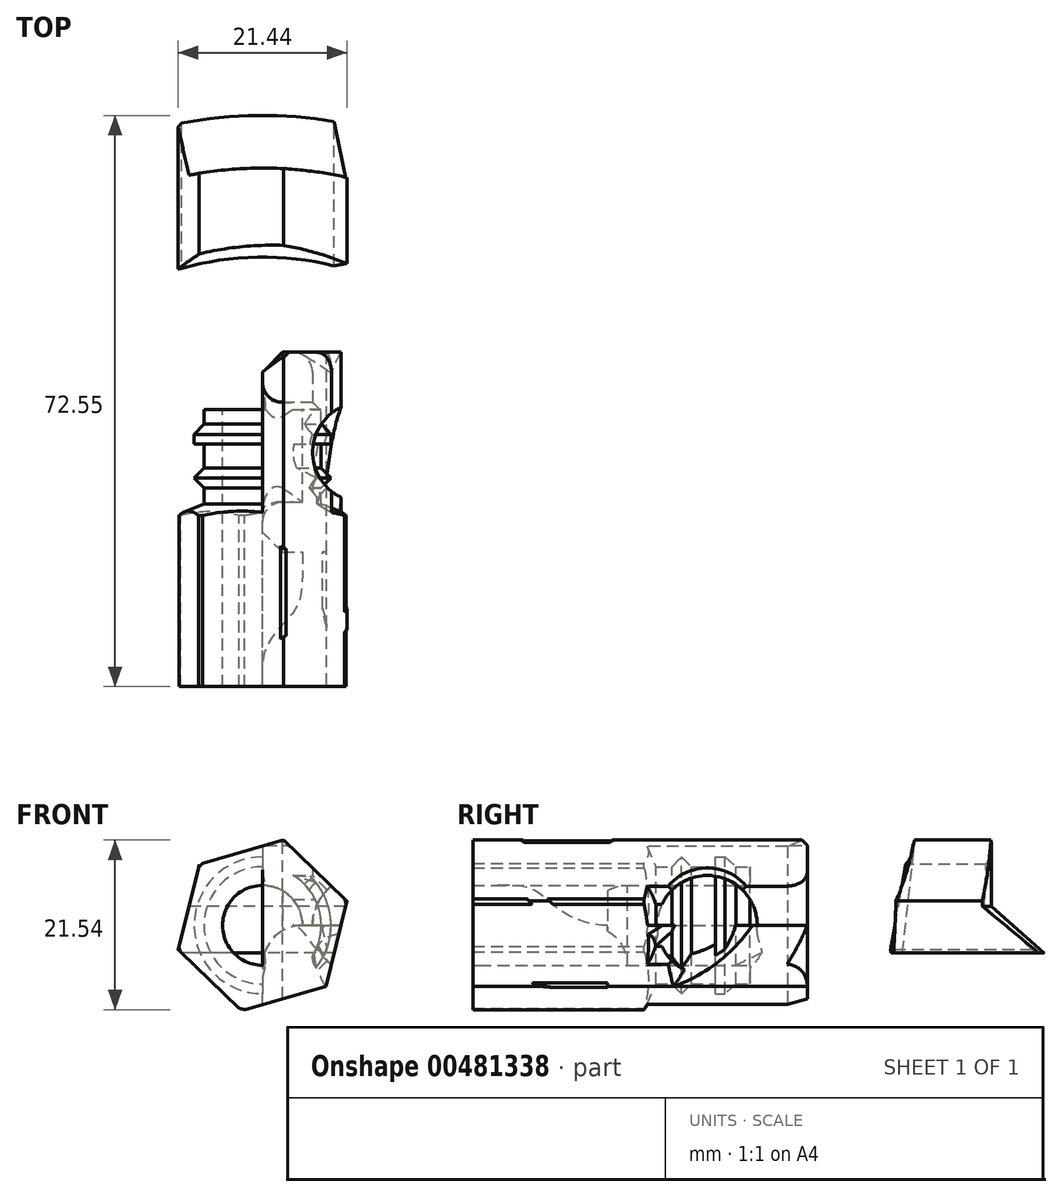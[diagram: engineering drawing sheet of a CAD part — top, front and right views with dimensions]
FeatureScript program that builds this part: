
annotation { "Feature Type Name" : "Feature", "Feature Type Description" : "" }
export const myFeature = defineFeature(function(context is Context, id is Id, definition is map)
    precondition{}
    {
        {
            var Q0;
            Q0=qCreatedBy(makeId("Top.planeOp"),FACE);
            var sketch = newSketch(context, id + "F0", { "sketchPlane" : qUnion([Q0])});
            skLineSegment(sketch, "E0.bottom", {"start": v(0, 0) * mm, "end": v(25.4, 0) * mm});
            skLineSegment(sketch, "E0.top", {"start": v(0, 25.4) * mm, "end": v(25.4, 25.4) * mm});
            skLineSegment(sketch, "E0.left", {"start": v(0, 0) * mm, "end": v(0, 25.4) * mm});
            skLineSegment(sketch, "E0.right", {"start": v(25.4, 0) * mm, "end": v(25.4, 25.4) * mm});
            skCircle(sketch, "E1", {"center": v(12.7, 12.7) * mm, "radius": 6.35 * mm});
            skPoint(sketch, "E1.centerSnap0", {"position": v(12.7, 0) * mm});
            skSolve(sketch);
        }
        {
            var Q0;
            Q0 = qSketchRegion(id + "F0", true);
            extrude(context, id + "F1", {"entities" : qUnion([Q0]), "endBound" : BoundingType.SYMMETRIC, "depth" : 25.4 * mm});
        }
        {
            var Q0;
            Q0=makeQuery(id+"F1.opExtrude","SWEPT_FACE",FACE,{"disambiguationData":[OSD([sQuery(id+"F0.wireOp",EDGE,"E0.right")])]});
            var sketch = newSketch(context, id + "F2", { "sketchPlane" : qUnion([Q0])});
            skCircle(sketch, "E2", {"center": v(12.7, 0) * mm, "radius": 6.35 * mm});
            skSolve(sketch);
        }
        {
            var Q0;
            Q0=makeQuery(id+"F2.imprint","IMPRINT",FACE,{"disambiguationData":[TD([[makeQuery(id+"F2.imprint","IMPRINT",EDGE,{"derivedFrom":sQuery(id+"F2.wireOp",EDGE,"E2")}),1.0]])]});
            extrude(context, id + "F3", {"entities" : qUnion([Q0]), "operationType" : NewBodyOperationType.REMOVE, "endBound" : BoundingType.THROUGH_ALL, "oppositeDirection" : true, "depth" : 25.4 * mm});
        }
        {
            var Q0;
            Q0=makeQuery(id+"F1.opExtrude","SWEPT_FACE",FACE,{"disambiguationData":[OSD([sQuery(id+"F0.wireOp",EDGE,"E0.bottom")])]});
            var sketch = newSketch(context, id + "F4", { "sketchPlane" : qUnion([Q0])});
            skCircle(sketch, "E3", {"center": v(12.7, 0) * mm, "radius": 6.35 * mm});
            skSolve(sketch);
        }
        {
            var Q0;
            Q0=makeQuery(id+"F4.imprint","IMPRINT",FACE,{"disambiguationData":[TD([[makeQuery(id+"F4.imprint","IMPRINT",EDGE,{"derivedFrom":sQuery(id+"F4.wireOp",EDGE,"E3")}),1.0]])]});
            extrude(context, id + "F5", {"entities" : qUnion([Q0]), "operationType" : NewBodyOperationType.REMOVE, "endBound" : BoundingType.THROUGH_ALL, "oppositeDirection" : true, "depth" : 25.4 * mm});
        }
        {
            var Q0;
            Q0=makeQuery(id+"F1.opExtrude","CAP_EDGE",EDGE,{"disambiguationData":[OSD([sQuery(id+"F0.wireOp",EDGE,"E0.bottom")])],"isStart":false});
            var Q1;
            Q1=makeQuery(id+"F1.opExtrude","CAP_EDGE",EDGE,{"disambiguationData":[OSD([sQuery(id+"F0.wireOp",EDGE,"E0.right")])],"isStart":false});
            var Q2;
            Q2=makeQuery(id+"F1.opExtrude","SWEPT_EDGE",EDGE,{"disambiguationData":[OSD([sQuery(id+"F0.wireOp",EDGE,"E0.bottom"),sQuery(id+"F0.wireOp",EDGE,"E0.right")])]});
            var Q3;
            Q3=makeQuery(id+"F1.opExtrude","CAP_EDGE",EDGE,{"disambiguationData":[OSD([sQuery(id+"F0.wireOp",EDGE,"E0.bottom")])],"isStart":true});
            var Q4;
            Q4=makeQuery(id+"F1.opExtrude","CAP_EDGE",EDGE,{"disambiguationData":[OSD([sQuery(id+"F0.wireOp",EDGE,"E0.right")])],"isStart":true});
            var Q5;
            Q5=makeQuery(id+"F1.opExtrude","SWEPT_EDGE",EDGE,{"disambiguationData":[OSD([sQuery(id+"F0.wireOp",EDGE,"E0.top"),sQuery(id+"F0.wireOp",EDGE,"E0.right")])]});
            var Q6;
            Q6=makeQuery(id+"F1.opExtrude","CAP_EDGE",EDGE,{"disambiguationData":[OSD([sQuery(id+"F0.wireOp",EDGE,"E0.top")])],"isStart":false});
            var Q7;
            Q7=makeQuery(id+"F1.opExtrude","SWEPT_EDGE",EDGE,{"disambiguationData":[OSD([sQuery(id+"F0.wireOp",EDGE,"E0.top"),sQuery(id+"F0.wireOp",EDGE,"E0.left")])]});
            var Q8;
            Q8=makeQuery(id+"F1.opExtrude","CAP_EDGE",EDGE,{"disambiguationData":[OSD([sQuery(id+"F0.wireOp",EDGE,"E0.top")])],"isStart":true});
            var Q9;
            Q9=makeQuery(id+"F1.opExtrude","CAP_EDGE",EDGE,{"disambiguationData":[OSD([sQuery(id+"F0.wireOp",EDGE,"E0.left")])],"isStart":false});
            var Q10;
            Q10=makeQuery(id+"F1.opExtrude","CAP_EDGE",EDGE,{"disambiguationData":[OSD([sQuery(id+"F0.wireOp",EDGE,"E0.left")])],"isStart":true});
            var Q11;
            Q11=makeQuery(id+"F1.opExtrude","SWEPT_EDGE",EDGE,{"disambiguationData":[OSD([sQuery(id+"F0.wireOp",EDGE,"E0.bottom"),sQuery(id+"F0.wireOp",EDGE,"E0.left")])]});
            chamfer(context, id + "F6", {"entities" : qUnion([Q0, Q1, Q2, Q3, Q4, Q5, Q6, Q7, Q8, Q9, Q10, Q11]), "width" : 2.54 * mm, "tangentPropagation" : true});
        }
        {
            var Q0;
            Q0 = qSketchRegion(id + "F0", true);
            var Q1;
            {var subQ0=sQuery(id+"F0.wireOp",EDGE,"E0.bottom");Q1=makeQuery(id+"F6.opChamfer","BLEND_EDGE",EDGE,{"blendedFrom":[makeQuery(id+"F1.opExtrude","CAP_EDGE",EDGE,{"disambiguationData":[OSD([subQ0])],"isStart":false}),makeQuery(id+"F1.opExtrude","SWEPT_FACE",FACE,{"disambiguationData":[OSD([subQ0])]})],"blendedInto":[makeQuery(id+"F1.opExtrude","SWEPT_FACE",FACE,{"disambiguationData":[OSD([subQ0])]})]});}
            revolve(context, id + "F7", {"entities" : qUnion([Q0]), "axis" : qUnion([Q1]), "revolveType" : RevolveType.ONE_DIRECTION, "angle" : 220 * degree});
        }
        {
            var Q0;
            Q0=makeQuery(id+"F7.opRevolve","SWEPT_EDGE",EDGE,{"disambiguationData":[OSD([sQuery(id+"F0.wireOp",EDGE,"E0.top"),sQuery(id+"F0.wireOp",EDGE,"E0.right")])]});
            var Q1;
            Q1=makeQuery(id+"F7.opRevolve","SWEPT_EDGE",EDGE,{"disambiguationData":[OSD([sQuery(id+"F0.wireOp",EDGE,"E0.top"),sQuery(id+"F0.wireOp",EDGE,"E0.left")])]});
            var Q2;
            Q2=makeQuery(id+"F7.opRevolve","SWEPT_EDGE",EDGE,{"disambiguationData":[OSD([sQuery(id+"F0.wireOp",EDGE,"E0.bottom"),sQuery(id+"F0.wireOp",EDGE,"E0.right")])]});
            var Q3;
            Q3=makeQuery(id+"F7.opRevolve","SWEPT_EDGE",EDGE,{"disambiguationData":[OSD([sQuery(id+"F0.wireOp",EDGE,"E0.bottom"),sQuery(id+"F0.wireOp",EDGE,"E0.left")])]});
            fillet(context, id + "F8", {"entities" : qUnion([Q0, Q1, Q2, Q3]), "radius" : 5.08 * mm, "tangentPropagation" : true, "allowEdgeOverflow" : false});
        }
        {
            var Q0;
            Q0=qCreatedBy(makeId("Right.planeOp"),FACE);
            var sketch = newSketch(context, id + "F9", { "sketchPlane" : qUnion([Q0])});
            skLineSegment(sketch, "E4", {"start": v(46.5, 50.21) * mm, "end": v(53.68, 41.23) * mm});
            skLineSegment(sketch, "E5", {"start": v(53.68, 41.23) * mm, "end": v(53.68, 32.24) * mm});
            skLineSegment(sketch, "E6", {"start": v(53.68, 32.24) * mm, "end": v(48.8, 28.13) * mm});
            skLineSegment(sketch, "E7", {"start": v(48.8, 28.13) * mm, "end": v(48.8, 2.44) * mm});
            skLineSegment(sketch, "E8", {"start": v(48.8, 2.44) * mm, "end": v(55.48, -3.47) * mm});
            skLineSegment(sketch, "E9", {"start": v(55.48, -3.47) * mm, "end": v(37.5, -3.47) * mm});
            skLineSegment(sketch, "E10", {"start": v(37.5, -3.47) * mm, "end": v(41.61, 33.78) * mm});
            skLineSegment(sketch, "E11", {"start": v(41.61, 33.78) * mm, "end": v(47.26, 37.89) * mm});
            skLineSegment(sketch, "E12", {"start": v(47.26, 37.89) * mm, "end": v(42.53, 44.4) * mm});
            skLineSegment(sketch, "E13", {"start": v(42.53, 44.4) * mm, "end": v(46.5, 50.21) * mm});
            skLineSegment(sketch, "E14", {"start": v(0, 58.43) * mm, "end": v(0, -37.89) * mm});
            skSolve(sketch);
        }
        {
            var Q0;
            Q0=makeQuery(id+"F9.imprint","IMPRINT",FACE,{"disambiguationData":[TD([[makeQuery(id+"F9.imprint","IMPRINT",EDGE,{"derivedFrom":sQuery(id+"F9.wireOp",EDGE,"E4")}),-1.0]])]});
            var Q1;
            Q1=sQuery(id+"F9.wireOp",EDGE,"E14");
            revolve(context, id + "F10", {"entities" : qUnion([Q0]), "axis" : qUnion([Q1]), "revolveType" : RevolveType.FULL});
        }
        {
            var Q0;
            Q0=qCreatedBy(makeId("Top.planeOp"),FACE);
            var sketch = newSketch(context, id + "F11", { "sketchPlane" : qUnion([Q0])});
            skLineSegment(sketch, "E15", {"start": v(-7.45, 18.12) * mm, "end": v(-7.45, 16.31) * mm});
            skLineSegment(sketch, "E16", {"start": v(-7.45, 16.31) * mm, "end": v(-8.7, 14.96) * mm});
            skLineSegment(sketch, "E17", {"start": v(-8.7, 14.96) * mm, "end": v(-8.7, 13.72) * mm});
            skLineSegment(sketch, "E18", {"start": v(-8.7, 13.72) * mm, "end": v(-7.45, 13.72) * mm});
            skLineSegment(sketch, "E19", {"start": v(-7.45, 13.72) * mm, "end": v(-7.45, 10.67) * mm});
            skLineSegment(sketch, "E20", {"start": v(-7.45, 10.67) * mm, "end": v(-8.7, 9.43) * mm});
            skLineSegment(sketch, "E21", {"start": v(-8.7, 9.43) * mm, "end": v(-7.45, 8.18) * mm});
            skLineSegment(sketch, "E22", {"start": v(-7.45, 8.18) * mm, "end": v(-7.45, 6.15) * mm});
            skLineSegment(sketch, "E23", {"start": v(-7.45, 6.15) * mm, "end": v(-10.95, 4.68) * mm});
            skLineSegment(sketch, "E24", {"start": v(-10.95, 4.68) * mm, "end": v(-10.95, 1.98) * mm});
            skLineSegment(sketch, "E25", {"start": v(-10.95, 1.98) * mm, "end": v(-5.08, 1.98) * mm});
            skLineSegment(sketch, "E26", {"start": v(-5.08, 1.98) * mm, "end": v(-5.08, 18.12) * mm});
            skLineSegment(sketch, "E27", {"start": v(-5.08, 18.12) * mm, "end": v(-7.45, 18.12) * mm});
            skLineSegment(sketch, "E28", {"start": v(0, 21.26) * mm, "end": v(0, -9.25) * mm});
            skSolve(sketch);
        }
        {
            var Q0;
            Q0=makeQuery(id+"F11.imprint","IMPRINT",FACE,{"disambiguationData":[TD([[makeQuery(id+"F11.imprint","IMPRINT",EDGE,{"derivedFrom":sQuery(id+"F11.wireOp",EDGE,"E15")}),1.0]])]});
            var Q1;
            Q1=sQuery(id+"F11.wireOp",EDGE,"E28");
            revolve(context, id + "F12", {"entities" : qUnion([Q0]), "axis" : qUnion([Q1]), "revolveType" : RevolveType.FULL});
        }
        {
            var Q0;
            Q0=makeQuery(id+"F12.opRevolve","SWEPT_FACE",FACE,{"disambiguationData":[OSD([sQuery(id+"F11.wireOp",EDGE,"E25")])]});
            extrude(context, id + "F13", {"entities" : qUnion([Q0]), "operationType" : NewBodyOperationType.ADD, "depth" : 19.05 * mm});
        }
        {
            var Q0;
            Q0=makeQuery(id+"F13.opExtrude","CAP_FACE",FACE,{"disambiguationData":[OSD([sQuery(id+"F11.wireOp",EDGE,"E25")])],"isStart":false});
            var sketch = newSketch(context, id + "F14", { "sketchPlane" : qUnion([Q0])});
            skCircle(sketch, "E29.cCircle", {"center": v(0, 0) * mm, "radius": 9.67 * mm, "construction": true});
            skLineSegment(sketch, "E29.0", {"start": v(-10.72, -3.1) * mm, "end": v(-8.04, 7.74) * mm});
            skLineSegment(sketch, "E29.1", {"start": v(-8.04, 7.74) * mm, "end": v(2.69, 10.83) * mm});
            skLineSegment(sketch, "E29.2", {"start": v(2.69, 10.83) * mm, "end": v(10.72, 3.1) * mm});
            skLineSegment(sketch, "E29.3", {"start": v(10.72, 3.1) * mm, "end": v(8.04, -7.74) * mm});
            skLineSegment(sketch, "E29.4", {"start": v(8.04, -7.74) * mm, "end": v(-2.69, -10.83) * mm});
            skLineSegment(sketch, "E29.5", {"start": v(-2.69, -10.83) * mm, "end": v(-10.72, -3.1) * mm});
            skPoint(sketch, "E29.0.midPoint", {"position": v(-9.38, 2.33) * mm});
            skSolve(sketch);
        }
        {
            var Q0;
            Q0 = qSketchRegion(id + "F14", true);
            extrude(context, id + "F15", {"entities" : qUnion([Q0]), "operationType" : NewBodyOperationType.INTERSECT, "oppositeDirection" : true, "depth" : 203.2 * mm});
        }
        {
            var Q0;
            Q0=makeQuery(id+"F5.boolean.opBoolean","INTERSECT",EDGE,{"derivedFrom":[makeQuery(id+"F1.opExtrude","SWEPT_FACE",FACE,{"disambiguationData":[OSD([sQuery(id+"F0.wireOp",EDGE,"E0.top")])]}),makeQuery(id+"F5.opExtrude","SWEPT_FACE",FACE,{"disambiguationData":[OSD([sQuery(id+"F4.wireOp",EDGE,"E3")])]})]});
            var Q1;
            Q1=makeQuery(id+"F3.boolean.opBoolean","INTERSECT",EDGE,{"derivedFrom":[makeQuery(id+"F1.opExtrude","SWEPT_FACE",FACE,{"disambiguationData":[OSD([sQuery(id+"F0.wireOp",EDGE,"E0.left")])]}),makeQuery(id+"F3.opExtrude","SWEPT_FACE",FACE,{"disambiguationData":[OSD([sQuery(id+"F2.wireOp",EDGE,"E2")])]})]});
            var Q2;
            Q2=makeQuery(id+"F1.opExtrude","CAP_EDGE",EDGE,{"disambiguationData":[OSD([sQuery(id+"F0.wireOp",EDGE,"E1")])],"isStart":false});
            var Q3;
            Q3=makeQuery(id+"F3.boolean.opBoolean","COPY",EDGE,{"derivedFrom":makeQuery(id+"F3.opExtrude","CAP_EDGE",EDGE,{"disambiguationData":[OSD([sQuery(id+"F2.wireOp",EDGE,"E2")])],"isStart":true})});
            var Q4;
            Q4=makeQuery(id+"F1.opExtrude","CAP_EDGE",EDGE,{"disambiguationData":[OSD([sQuery(id+"F0.wireOp",EDGE,"E1")])],"isStart":true});
            var Q5;
            Q5=makeQuery(id+"F5.boolean.opBoolean","COPY",EDGE,{"derivedFrom":makeQuery(id+"F5.opExtrude","CAP_EDGE",EDGE,{"disambiguationData":[OSD([sQuery(id+"F4.wireOp",EDGE,"E3")])],"isStart":true})});
            fillet(context, id + "F16", {"entities" : qUnion([Q0, Q1, Q2, Q3, Q4, Q5]), "radius" : 2.54 * mm, "tangentPropagation" : true, "allowEdgeOverflow" : false});
        }
    });
